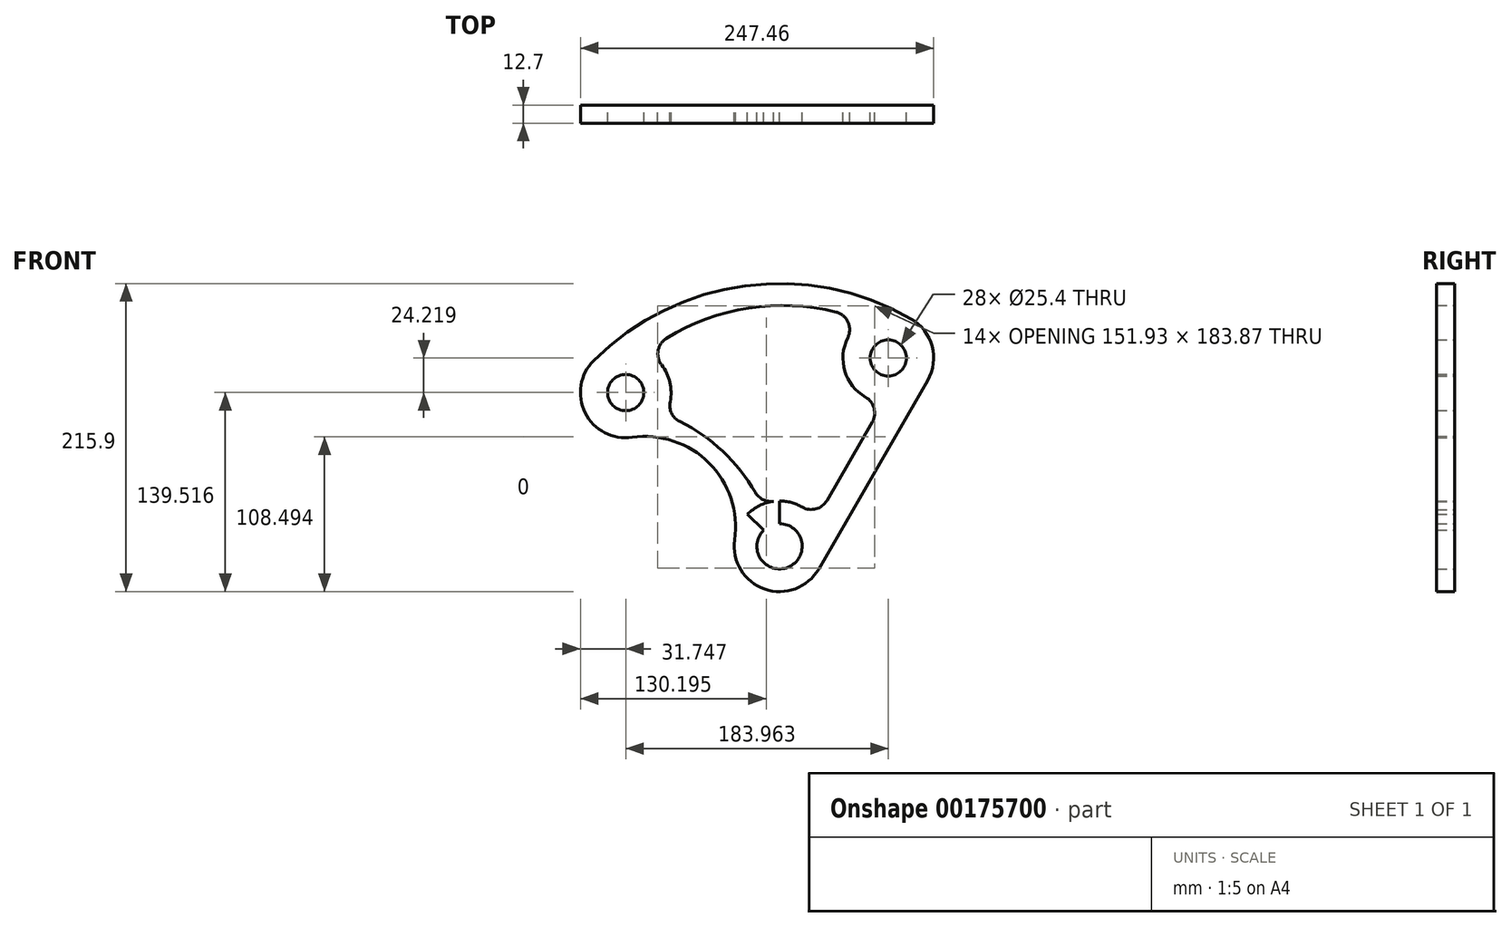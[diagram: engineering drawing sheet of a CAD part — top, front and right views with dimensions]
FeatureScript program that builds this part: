
annotation { "Feature Type Name" : "Feature", "Feature Type Description" : "" }
export const myFeature = defineFeature(function(context is Context, id is Id, definition is map)
    precondition{}
    {
        {
            var Q0;
            Q0=qCreatedBy(makeId("Front.planeOp"),FACE);
            var sketch = newSketch(context, id + "F0", { "sketchPlane" : qUnion([Q0])});
            skCircle(sketch, "E0", {"center": v(-107.76, 109.09) * mm, "radius": 12.7 * mm});
            skCircle(sketch, "E1", {"center": v(76.2, 133.3) * mm, "radius": 12.7 * mm});
            skCircle(sketch, "E2", {"center": v(0, 1.32) * mm, "radius": 15.88 * mm});
            skLineSegment(sketch, "E3", {"start": v(0, 1.32) * mm, "end": v(76.2, 133.3) * mm});
            skLineSegment(sketch, "E4", {"start": v(0, 1.32) * mm, "end": v(0, 49.49) * mm});
            skLineSegment(sketch, "E5", {"start": v(0, 1.32) * mm, "end": v(-107.76, 109.09) * mm});
            skCircle(sketch, "E6", {"center": v(-107.76, 109.09) * mm, "radius": 31.75 * mm});
            skCircle(sketch, "E7", {"center": v(76.2, 133.3) * mm, "radius": 31.75 * mm});
            skCircle(sketch, "E8", {"center": v(0, 1.32) * mm, "radius": 31.75 * mm});
            skLineSegment(sketch, "E9", {"start": v(27.5, -14.55) * mm, "end": v(103.7, 117.43) * mm});
            skArc(sketch, "E10", {"start": v(92.07, 160.8) * mm, "mid": v(-24.04, 183.9) * mm, "end": v(-130.21, 131.54) * mm});
            skArc(sketch, "E11", {"start": v(-31.43, 5.81) * mm, "mid": v(-49.4, 59.7) * mm, "end": v(-103.27, 77.65) * mm});
            skLineSegment(sketch, "E12", {"start": v(-130.21, 131.54) * mm, "end": v(-107.76, 109.09) * mm});
            skLineSegment(sketch, "E13", {"start": v(92.08, 160.8) * mm, "end": v(76.2, 133.3) * mm});
            skLineSegment(sketch, "E14", {"start": v(33.22, 33.47) * mm, "end": v(64.97, 88.46) * mm});
            skArc(sketch, "E15", {"start": v(39.54, 165.5) * mm, "mid": v(-21.74, 168.34) * mm, "end": v(-79.27, 147.05) * mm});
            skPoint(sketch, "E15.endSnap0", {"position": v(84.14, 147.05) * mm});
            skArc(sketch, "E16", {"start": v(-16.86, 39.03) * mm, "mid": v(-39.7, 67.81) * mm, "end": v(-69.86, 88.77) * mm});
            skArc(sketch, "E17", {"start": v(15.87, 28.82) * mm, "mid": v(25.51, 27.55) * mm, "end": v(33.22, 33.47) * mm});
            skArc(sketch, "E18", {"start": v(64.97, 88.46) * mm, "mid": v(66.24, 98.1) * mm, "end": v(60.33, 105.8) * mm});
            skArc(sketch, "E19", {"start": v(47.8, 147.5) * mm, "mid": v(47.99, 158.48) * mm, "end": v(39.54, 165.5) * mm});
            skArc(sketch, "E20", {"start": v(-79.27, 147.05) * mm, "mid": v(-85.08, 138.52) * mm, "end": v(-82.64, 128.5) * mm});
            skArc(sketch, "E21", {"start": v(-76.66, 102.7) * mm, "mid": v(-75.63, 94.58) * mm, "end": v(-69.86, 88.77) * mm});
            skArc(sketch, "E22", {"start": v(-16.86, 39.03) * mm, "mid": v(-11.47, 33.99) * mm, "end": v(-4.2, 32.8) * mm});
            skSolve(sketch);
        }
        {
            var Q0;
            Q0=makeQuery(id+"F0.imprint","IMPRINT",FACE,{"disambiguationData":[TD([[makeQuery(id+"F0.imprint","IMPRINT",EDGE,{"derivedFrom":sQuery(id+"F0.wireOp",EDGE,"E16")}),1.0]])]});
            var Q1;
            {var subQ0=sQuery(id+"F0.wireOp",EDGE,"E11");var subQ1=sQuery(id+"F0.wireOp",EDGE,"E5");var subQ2=makeQuery(id+"F0.imprint","INTERSECT",VERTEX,{"disambiguationData":[OD(1.0)],"derivedFrom":[subQ1,subQ0]});Q1=makeQuery(id+"F0.imprint","IMPRINT",FACE,{"disambiguationData":[TD([[makeQuery(id+"F0.imprint","IMPRINT",EDGE,{"disambiguationData":[TD([[subQ2,-1.0]])],"derivedFrom":subQ1}),1.0]])]});}
            var Q2;
            {var subQ0=sQuery(id+"F0.wireOp",EDGE,"E11");var subQ1=sQuery(id+"F0.wireOp",EDGE,"E5");var subQ2=makeQuery(id+"F0.imprint","INTERSECT",VERTEX,{"disambiguationData":[OD(0.0)],"derivedFrom":[subQ1,subQ0]});Q2=makeQuery(id+"F0.imprint","IMPRINT",FACE,{"disambiguationData":[TD([[makeQuery(id+"F0.imprint","IMPRINT",EDGE,{"disambiguationData":[TD([[subQ2,1.0]])],"derivedFrom":subQ1}),1.0]])]});}
            var Q3;
            {var subQ0=sQuery(id+"F0.wireOp",EDGE,"E9");Q3=makeQuery(id+"F0.imprint","IMPRINT",FACE,{"disambiguationData":[TD([[makeQuery(id+"F0.imprint","IMPRINT",EDGE,{"derivedFrom":subQ0}),1.0]])]});}
            var Q4;
            {var subQ0=sQuery(id+"F0.wireOp",EDGE,"E10");Q4=makeQuery(id+"F0.imprint","IMPRINT",FACE,{"disambiguationData":[TD([[makeQuery(id+"F0.imprint","IMPRINT",EDGE,{"derivedFrom":subQ0}),1.0]])]});}
            var Q5;
            {var subQ2=sQuery(id+"F0.wireOp",EDGE,"E5");var subQ4=sQuery(id+"F0.wireOp",EDGE,"E0");var subQ5=makeQuery(id+"F0.imprint","INTERSECT",VERTEX,{"derivedFrom":[subQ4,subQ2]});Q5=makeQuery(id+"F0.imprint","IMPRINT",FACE,{"disambiguationData":[TD([[makeQuery(id+"F0.imprint","IMPRINT",EDGE,{"disambiguationData":[TD([[subQ5,-1.0]])],"derivedFrom":subQ4}),-1.0]])]});}
            var Q6;
            {var subQ4=sQuery(id+"F0.wireOp",EDGE,"E3");var subQ6=sQuery(id+"F0.wireOp",EDGE,"E1");var subQ7=makeQuery(id+"F0.imprint","INTERSECT",VERTEX,{"derivedFrom":[subQ6,subQ4]});Q6=makeQuery(id+"F0.imprint","IMPRINT",FACE,{"disambiguationData":[TD([[makeQuery(id+"F0.imprint","IMPRINT",EDGE,{"disambiguationData":[TD([[subQ7,-1.0]])],"derivedFrom":subQ6}),-1.0]])]});}
            var Q7;
            {var subQ1=sQuery(id+"F0.wireOp",EDGE,"E3");var subQ6=sQuery(id+"F0.wireOp",EDGE,"E1");var subQ7=makeQuery(id+"F0.imprint","INTERSECT",VERTEX,{"derivedFrom":[subQ6,subQ1]});Q7=makeQuery(id+"F0.imprint","IMPRINT",FACE,{"disambiguationData":[TD([[makeQuery(id+"F0.imprint","IMPRINT",EDGE,{"disambiguationData":[TD([[subQ7,1.0]])],"derivedFrom":subQ6}),-1.0]])]});}
            var Q8;
            {var subQ4=sQuery(id+"F0.wireOp",EDGE,"E5");var subQ6=sQuery(id+"F0.wireOp",EDGE,"E0");var subQ7=makeQuery(id+"F0.imprint","INTERSECT",VERTEX,{"derivedFrom":[subQ6,subQ4]});Q8=makeQuery(id+"F0.imprint","IMPRINT",FACE,{"disambiguationData":[TD([[makeQuery(id+"F0.imprint","IMPRINT",EDGE,{"disambiguationData":[TD([[subQ7,1.0]])],"derivedFrom":subQ6}),-1.0]])]});}
            var Q9;
            {var subQ2=sQuery(id+"F0.wireOp",EDGE,"E4");var subQ5=sQuery(id+"F0.wireOp",EDGE,"E2");var subQ8=makeQuery(id+"F0.imprint","INTERSECT",VERTEX,{"derivedFrom":[subQ5,subQ2]});Q9=makeQuery(id+"F0.imprint","IMPRINT",FACE,{"disambiguationData":[TD([[makeQuery(id+"F0.imprint","IMPRINT",EDGE,{"disambiguationData":[TD([[subQ8,-1.0]])],"derivedFrom":subQ5}),-1.0]])]});}
            var Q10;
            {var subQ0=sQuery(id+"F0.wireOp",EDGE,"E4");var subQ1=sQuery(id+"F0.wireOp",EDGE,"E2");var subQ2=makeQuery(id+"F0.imprint","INTERSECT",VERTEX,{"derivedFrom":[subQ1,subQ0]});Q10=makeQuery(id+"F0.imprint","IMPRINT",FACE,{"disambiguationData":[TD([[makeQuery(id+"F0.imprint","IMPRINT",EDGE,{"disambiguationData":[TD([[subQ2,1.0]])],"derivedFrom":subQ1}),-1.0]])]});}
            var Q11;
            {var subQ4=sQuery(id+"F0.wireOp",EDGE,"E2");var subQ6=sQuery(id+"F0.wireOp",EDGE,"E3");var subQ7=makeQuery(id+"F0.imprint","INTERSECT",VERTEX,{"derivedFrom":[subQ4,subQ6]});Q11=makeQuery(id+"F0.imprint","IMPRINT",FACE,{"disambiguationData":[TD([[makeQuery(id+"F0.imprint","IMPRINT",EDGE,{"disambiguationData":[TD([[subQ7,1.0]])],"derivedFrom":subQ4}),-1.0]])]});}
            extrude(context, id + "F1", {"entities" : qUnion([Q0, Q1, Q2, Q3, Q4, Q5, Q6, Q7, Q8, Q9, Q10, Q11]), "depth" : 12.7 * mm});
        }
    });
